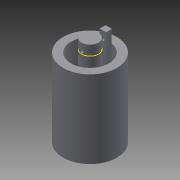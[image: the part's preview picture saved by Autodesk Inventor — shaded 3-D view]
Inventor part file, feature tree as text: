
AUTODESK INVENTOR PART (.ipt)
format: ipt  version: 2013 SP2 (Build 170200200, 200)  size: 163,328 bytes
history: native  units: in
note: dims shown in document units (in); Inventor stores cm internally (conversion verified against a paired STEP export)
features: extrude x10, sketch x10
ambient origin geometry x8: Origin, YZ Plane, XZ Plane, XY Plane, X Axis, Y Axis, Z Axis, Center Point
feature tree (20):
  extrude  "Extrusion2"  Depth=0.3307in
  extrude  "Extrusion3"  Depth=0.1732in
  extrude  "Extrusion4"  Depth=0.388in
  extrude  "Extrusion5"  Depth=0.4724in TaperAngle=0.0deg
  extrude  "Extrusion6"  Depth=0.388in
  extrude  "Extrusion7"  Depth=0.1in TaperAngle=0.0deg
  sketch  "Sketch8"  dims[d38=0.33in d39=0.0in d41=0.1in d42=0.0in]
  extrude  "Extrusion8"  Depth=0.03in TaperAngle=0.0deg
  extrude  "Extrusion9"  Depth=0.031in
  extrude  "Extrusion10"  [1 undecoded]
  extrude  "Extrusion11"  [1 undecoded]
  sketch  "Sketch1"  dims[d5=0.5512in d8=0.3307in]
  sketch  "Sketch3"  dims[d9=0.3543in d10=0.0in d11=0.1732in]
  sketch  "Sketch5"  dims[d12=0.4724in d13=0.0in d14=0.388in]
  sketch  "Sketch6"  dims[d15=0.4724in d16=0.0in d17=0.4724in d18=0.0394in d19=0.0in d20=0.0in]
  sketch  "Sketch7"  dims[d21=0.3543in d22=0.0in d37=0.388in]
  sketch  "Sketch9"  dims[d43=0.1in d44=0.0in d45=0.03in d46=0.0in]
  sketch  "Sketch10"  dims[d47=1.0in d48=1.0in d49=0.0in d50=0.0in d53=0.031in]
  sketch  "Sketch11"
  sketch  "Sketch12"
note: 2 required parameter values undecoded (feature->parameter linkage not recoverable at this tier; creation-order binding heuristic only, values carry confidence <= 0.55)
